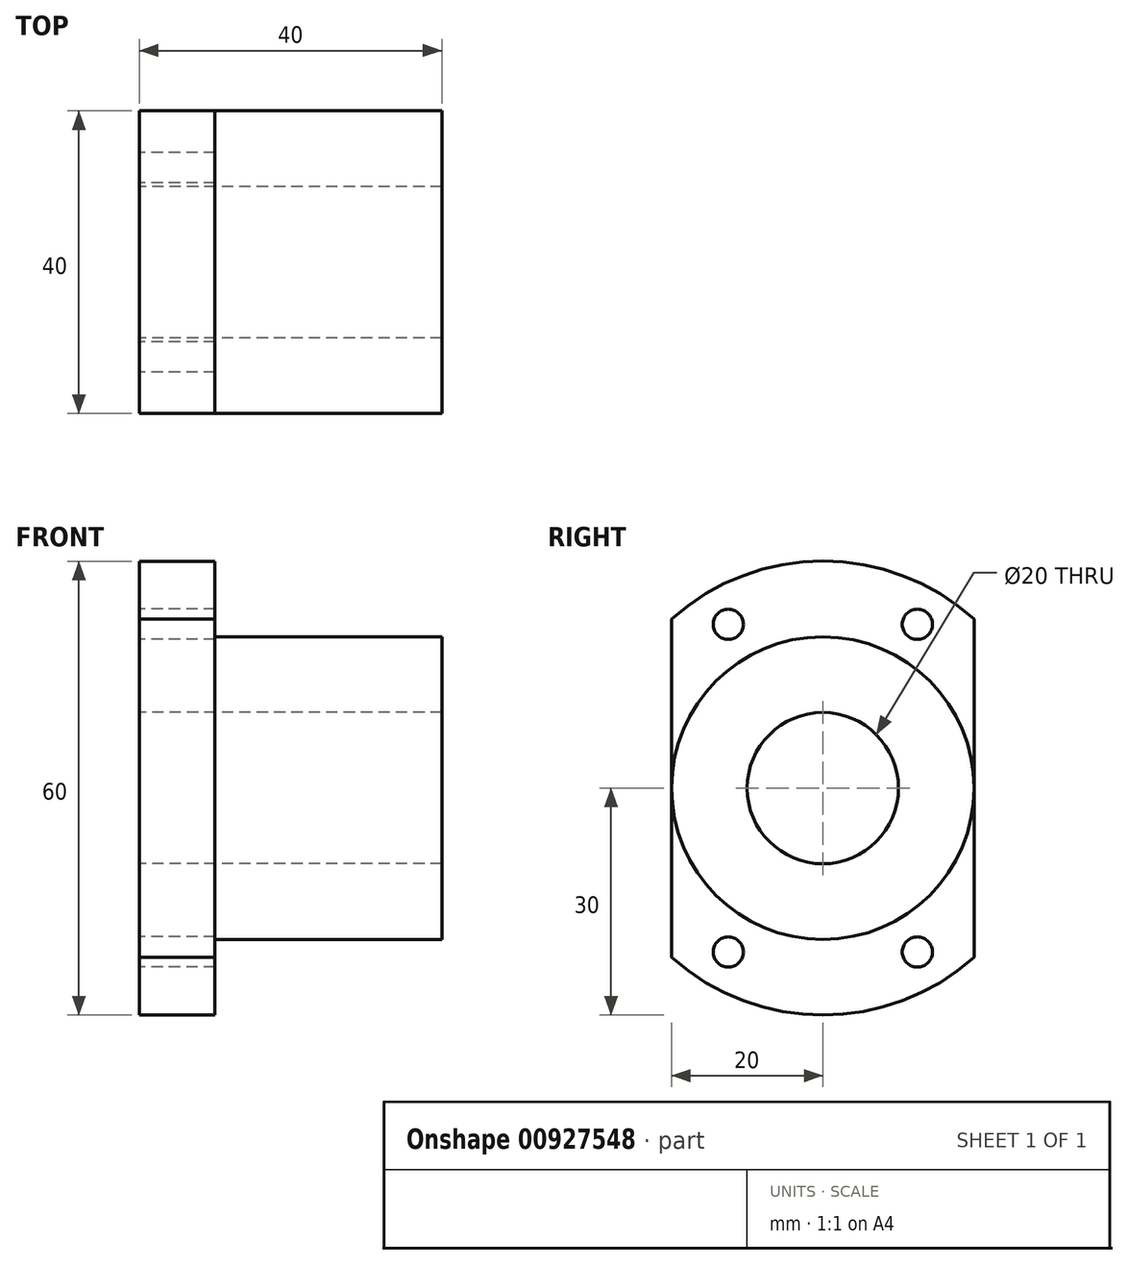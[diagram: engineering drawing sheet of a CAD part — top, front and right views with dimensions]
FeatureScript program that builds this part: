
annotation { "Feature Type Name" : "Feature", "Feature Type Description" : "" }
export const myFeature = defineFeature(function(context is Context, id is Id, definition is map)
    precondition{}
    {
        {
            var Q0;
            Q0=qCreatedBy(makeId("Right.planeOp"),FACE);
            var sketch = newSketch(context, id + "F0", { "sketchPlane" : qUnion([Q0])});
            skCircle(sketch, "E0", {"center": v(0, 0) * mm, "radius": 30 * mm});
            skSolve(sketch);
        }
        {
            var Q0;
            Q0 = qSketchRegion(id + "F0", true);
            extrude(context, id + "F1", {"entities" : qUnion([Q0]), "oppositeDirection" : true, "depth" : 40 * mm, "offsetDistance" : 25 * mm});
        }
        {
            var Q0;
            Q0=makeQuery(id+"F1.opExtrude","CAP_FACE",FACE,{"disambiguationData":[OSD([sQuery(id+"F0.wireOp",EDGE,"E0")])],"isStart":true});
            var sketch = newSketch(context, id + "F2", { "sketchPlane" : qUnion([Q0])});
            skCircle(sketch, "E1", {"center": v(0, 0) * mm, "radius": 20 * mm});
            skSolve(sketch);
        }
        {
            var Q0;
            Q0=makeQuery(id+"F2.imprint","IMPRINT",FACE,{"disambiguationData":[TD([[makeQuery(id+"F2.imprint","IMPRINT",EDGE,{"derivedFrom":sQuery(id+"F2.wireOp",EDGE,"E1")}),-1.0]])]});
            extrude(context, id + "F3", {"entities" : qUnion([Q0]), "operationType" : NewBodyOperationType.REMOVE, "oppositeDirection" : true, "depth" : 30 * mm, "offsetDistance" : 25 * mm});
        }
        {
            var Q0;
            Q0=makeQuery(id+"F1.opExtrude","CAP_FACE",FACE,{"disambiguationData":[OSD([sQuery(id+"F0.wireOp",EDGE,"E0")])],"isStart":false});
            var sketch = newSketch(context, id + "F4", { "sketchPlane" : qUnion([Q0])});
            skLineSegment(sketch, "E2", {"start": v(0, 59.78) * mm, "end": v(0, -59.55) * mm, "construction": true});
            skLineSegment(sketch, "E3", {"start": v(-74.6, 0) * mm, "end": v(84.94, 0) * mm, "construction": true});
            skLineSegment(sketch, "E4", {"start": v(20, 61.12) * mm, "end": v(20, -51.01) * mm});
            skLineSegment(sketch, "E5.MirrorCS", {"start": v(-20, 61.12) * mm, "end": v(-20, -51.01) * mm});
            skSolve(sketch);
        }
        {
            var Q0;
            {var subQ0=sQuery(id+"F4.wireOp",EDGE,"E5.MirrorCS");var subQ1=makeQuery(id+"F1.opExtrude","CAP_EDGE",EDGE,{"disambiguationData":[OSD([sQuery(id+"F0.wireOp",EDGE,"E0")])],"isStart":false});var subQ2=makeQuery(id+"F4.imprint","INTERSECT",VERTEX,{"disambiguationData":[OD(0.0)],"derivedFrom":[subQ1,subQ0]});Q0=makeQuery(id+"F4.imprint","IMPRINT",FACE,{"disambiguationData":[TD([[makeQuery(id+"F4.imprint","IMPRINT",EDGE,{"disambiguationData":[TD([[subQ2,1.0]])],"derivedFrom":subQ0}),-1.0]])]});}
            var Q1;
            {var subQ0=sQuery(id+"F4.wireOp",EDGE,"E4");var subQ1=makeQuery(id+"F1.opExtrude","CAP_EDGE",EDGE,{"disambiguationData":[OSD([sQuery(id+"F0.wireOp",EDGE,"E0")])],"isStart":false});var subQ2=makeQuery(id+"F4.imprint","INTERSECT",VERTEX,{"disambiguationData":[OD(0.0)],"derivedFrom":[subQ1,subQ0]});Q1=makeQuery(id+"F4.imprint","IMPRINT",FACE,{"disambiguationData":[TD([[makeQuery(id+"F4.imprint","IMPRINT",EDGE,{"disambiguationData":[TD([[subQ2,1.0]])],"derivedFrom":subQ0}),1.0]])]});}
            extrude(context, id + "F5", {"entities" : qUnion([Q0, Q1]), "operationType" : NewBodyOperationType.REMOVE, "endBound" : BoundingType.THROUGH_ALL, "oppositeDirection" : true, "depth" : 25 * mm, "offsetDistance" : 25 * mm});
        }
        {
            var Q0;
            Q0=makeQuery(id+"F1.opExtrude","CAP_FACE",FACE,{"disambiguationData":[OSD([sQuery(id+"F0.wireOp",EDGE,"E0")])],"isStart":false});
            var sketch = newSketch(context, id + "F6", { "sketchPlane" : qUnion([Q0])});
            skLineSegment(sketch, "E6", {"start": v(-39.8, 0) * mm, "end": v(46.02, 0) * mm, "construction": true});
            skLineSegment(sketch, "E7", {"start": v(0, 47.72) * mm, "end": v(0, -51.3) * mm, "construction": true});
            skPoint(sketch, "E7.endSnap0", {"position": v(0, -30) * mm});
            skCircle(sketch, "E8", {"center": v(0, 0) * mm, "radius": 25 * mm, "construction": true});
            skCircle(sketch, "E9", {"center": v(12.5, 21.65) * mm, "radius": 2 * mm});
            skLineSegment(sketch, "E10", {"start": v(0, 0) * mm, "end": v(24.75, 42.87) * mm, "construction": true});
            skCircle(sketch, "E11.MirrorC", {"center": v(-12.5, 21.65) * mm, "radius": 2 * mm});
            skCircle(sketch, "E12.MirrorC", {"center": v(12.5, -21.65) * mm, "radius": 2 * mm});
            skCircle(sketch, "E13.MirrorC", {"center": v(-12.5, -21.65) * mm, "radius": 2 * mm});
            skSolve(sketch);
        }
        {
            var Q0;
            Q0 = qSketchRegion(id + "F6", true);
            extrude(context, id + "F7", {"entities" : qUnion([Q0]), "operationType" : NewBodyOperationType.REMOVE, "endBound" : BoundingType.THROUGH_ALL, "oppositeDirection" : true, "depth" : 25 * mm, "offsetDistance" : 25 * mm});
        }
        {
            var Q0;
            Q0=makeQuery(id+"F1.opExtrude","CAP_FACE",FACE,{"disambiguationData":[OSD([sQuery(id+"F0.wireOp",EDGE,"E0")])],"isStart":false});
            var sketch = newSketch(context, id + "F8", { "sketchPlane" : qUnion([Q0])});
            skCircle(sketch, "E14", {"center": v(0, 0) * mm, "radius": 10 * mm});
            skSolve(sketch);
        }
        {
            var Q0;
            Q0 = qSketchRegion(id + "F8", true);
            extrude(context, id + "F9", {"entities" : qUnion([Q0]), "operationType" : NewBodyOperationType.REMOVE, "endBound" : BoundingType.THROUGH_ALL, "oppositeDirection" : true, "depth" : 25 * mm, "offsetDistance" : 25 * mm});
        }
    });
